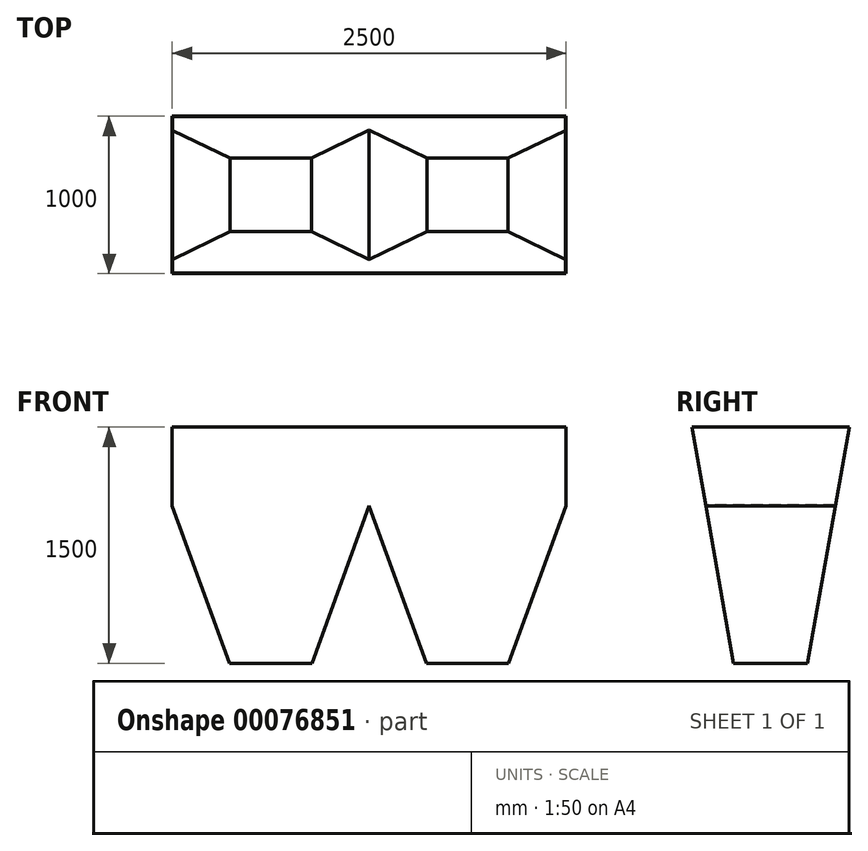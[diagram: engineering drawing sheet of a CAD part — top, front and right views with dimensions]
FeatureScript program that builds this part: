
annotation { "Feature Type Name" : "Feature", "Feature Type Description" : "" }
export const myFeature = defineFeature(function(context is Context, id is Id, definition is map)
    precondition{}
    {
        {
            var Q0;
            Q0=qCreatedBy(makeId("Top.planeOp"),FACE);
            var sketch = newSketch(context, id + "F0", { "sketchPlane" : qUnion([Q0])});
            skLineSegment(sketch, "E0.bottom", {"start": v(-1250, 500) * mm, "end": v(1250, 500) * mm});
            skLineSegment(sketch, "E0.top", {"start": v(-1250, -500) * mm, "end": v(1250, -500) * mm});
            skLineSegment(sketch, "E0.left", {"start": v(-1250, 500) * mm, "end": v(-1250, -500) * mm});
            skLineSegment(sketch, "E0.right", {"start": v(1250, 500) * mm, "end": v(1250, -500) * mm});
            skPoint(sketch, "E0.middle", {"position": v(0, 0) * mm});
            skSolve(sketch);
        }
        {
            var Q0;
            Q0=makeQuery(id+"F0.imprint","IMPRINT",FACE,{"disambiguationData":[TD([[makeQuery(id+"F0.imprint","IMPRINT",EDGE,{"derivedFrom":sQuery(id+"F0.wireOp",EDGE,"E0.bottom")}),-1.0]])]});
            extrude(context, id + "F1", {"entities" : qUnion([Q0]), "depth" : 1500 * mm});
        }
        {
            var Q0;
            Q0=makeQuery(id+"F1.opExtrude","SWEPT_FACE",FACE,{"disambiguationData":[OSD([sQuery(id+"F0.wireOp",EDGE,"E0.top")])]});
            var sketch = newSketch(context, id + "F2", { "sketchPlane" : qUnion([Q0])});
            skLineSegment(sketch, "E1", {"start": v(-1250, 1000) * mm, "end": v(-886.03, 0) * mm});
            skLineSegment(sketch, "E2", {"start": v(-886.03, 0) * mm, "end": v(-1250, 0) * mm});
            skLineSegment(sketch, "E3", {"start": v(-1250, 0) * mm, "end": v(-1250, 1000) * mm});
            skLineSegment(sketch, "E4", {"start": v(-1250, 1000) * mm, "end": v(1250, 1000) * mm, "construction": true});
            skLineSegment(sketch, "E5", {"start": v(1250, 1000) * mm, "end": v(886.03, 0) * mm});
            skLineSegment(sketch, "E6", {"start": v(886.03, 0) * mm, "end": v(1250, 0) * mm});
            skLineSegment(sketch, "E7", {"start": v(1250, 0) * mm, "end": v(1250, 1000) * mm});
            skLineSegment(sketch, "E8", {"start": v(-363.97, 0) * mm, "end": v(0, 1000) * mm});
            skLineSegment(sketch, "E9", {"start": v(0, 1000) * mm, "end": v(363.97, 0) * mm});
            skLineSegment(sketch, "E10", {"start": v(363.97, 0) * mm, "end": v(-363.97, 0) * mm});
            skLineSegment(sketch, "E11", {"start": v(0, 1000) * mm, "end": v(0, 1500) * mm, "construction": true});
            skSolve(sketch);
        }
        {
            var Q0;
            Q0=makeQuery(id+"F2.imprint","IMPRINT",FACE,{"disambiguationData":[TD([[makeQuery(id+"F2.imprint","IMPRINT",EDGE,{"derivedFrom":sQuery(id+"F2.wireOp",EDGE,"E1")}),-1.0]])]});
            var Q1;
            Q1=makeQuery(id+"F2.imprint","IMPRINT",FACE,{"disambiguationData":[TD([[makeQuery(id+"F2.imprint","IMPRINT",EDGE,{"derivedFrom":sQuery(id+"F2.wireOp",EDGE,"E8")}),-1.0]])]});
            var Q2;
            Q2=makeQuery(id+"F2.imprint","IMPRINT",FACE,{"disambiguationData":[TD([[makeQuery(id+"F2.imprint","IMPRINT",EDGE,{"derivedFrom":sQuery(id+"F2.wireOp",EDGE,"E5")}),1.0]])]});
            extrude(context, id + "F3", {"entities" : qUnion([Q0, Q1, Q2]), "operationType" : NewBodyOperationType.REMOVE, "endBound" : BoundingType.THROUGH_ALL, "oppositeDirection" : true, "depth" : 25 * mm});
        }
        {
            var Q0;
            Q0=makeQuery(id+"F1.opExtrude","SWEPT_FACE",FACE,{"disambiguationData":[OSD([sQuery(id+"F0.wireOp",EDGE,"E0.left")])]});
            var sketch = newSketch(context, id + "F4", { "sketchPlane" : qUnion([Q0])});
            skLineSegment(sketch, "E12", {"start": v(-500, 1500) * mm, "end": v(-235.5, 0) * mm});
            skLineSegment(sketch, "E13", {"start": v(-235.5, 0) * mm, "end": v(-500, 0) * mm});
            skLineSegment(sketch, "E14", {"start": v(-500, 0) * mm, "end": v(-500, 1500) * mm});
            skLineSegment(sketch, "E15.MirrorCS", {"start": v(500, 1500) * mm, "end": v(235.5, 0) * mm});
            skLineSegment(sketch, "E16.MirrorCS", {"start": v(235.5, 0) * mm, "end": v(500, 0) * mm});
            skLineSegment(sketch, "E17.MirrorCS", {"start": v(500, 0) * mm, "end": v(500, 1500) * mm});
            skSolve(sketch);
        }
        {
            var Q0;
            {var subQ0=sQuery(id+"F4.wireOp",EDGE,"E13");Q0=makeQuery(id+"F4.imprint","IMPRINT",FACE,{"disambiguationData":[TD([[makeQuery(id+"F4.imprint","IMPRINT",EDGE,{"derivedFrom":subQ0}),-1.0]])]});}
            var Q1;
            {var subQ0=sQuery(id+"F4.wireOp",EDGE,"E14");var subQ1=sQuery(id+"F4.wireOp",EDGE,"E12");var subQ2=sQuery(id+"F0.wireOp",EDGE,"E0.left");var subQ3=makeQuery(id+"F4.imprint","INTERSECT",VERTEX,{"derivedFrom":[makeQuery(id+"F1.opExtrude","CAP_EDGE",EDGE,{"disambiguationData":[OSD([subQ2])],"isStart":false}),subQ1,subQ0]});Q1=makeQuery(id+"F4.imprint","IMPRINT",FACE,{"disambiguationData":[TD([[makeQuery(id+"F4.imprint","IMPRINT",EDGE,{"disambiguationData":[TD([[subQ3,-1.0]])],"derivedFrom":subQ1}),-1.0]])]});}
            var Q2;
            {var subQ0=sQuery(id+"F4.wireOp",EDGE,"E16.MirrorCS");Q2=makeQuery(id+"F4.imprint","IMPRINT",FACE,{"disambiguationData":[TD([[makeQuery(id+"F4.imprint","IMPRINT",EDGE,{"derivedFrom":subQ0}),1.0]])]});}
            var Q3;
            {var subQ0=sQuery(id+"F4.wireOp",EDGE,"E17.MirrorCS");var subQ1=sQuery(id+"F4.wireOp",EDGE,"E15.MirrorCS");var subQ2=sQuery(id+"F0.wireOp",EDGE,"E0.left");var subQ3=makeQuery(id+"F4.imprint","INTERSECT",VERTEX,{"derivedFrom":[makeQuery(id+"F1.opExtrude","CAP_EDGE",EDGE,{"disambiguationData":[OSD([subQ2])],"isStart":false}),subQ1,subQ0]});Q3=makeQuery(id+"F4.imprint","IMPRINT",FACE,{"disambiguationData":[TD([[makeQuery(id+"F4.imprint","IMPRINT",EDGE,{"disambiguationData":[TD([[subQ3,-1.0]])],"derivedFrom":subQ1}),1.0]])]});}
            extrude(context, id + "F5", {"entities" : qUnion([Q0, Q1, Q2, Q3]), "operationType" : NewBodyOperationType.REMOVE, "endBound" : BoundingType.THROUGH_ALL, "oppositeDirection" : true, "depth" : 25 * mm});
        }
        {
            var Q0;
            Q0=makeQuery(id+"F1.opExtrude","CAP_FACE",FACE,{"disambiguationData":[OSD([sQuery(id+"F0.wireOp",EDGE,"E0.bottom"),sQuery(id+"F0.wireOp",EDGE,"E0.top"),sQuery(id+"F0.wireOp",EDGE,"E0.left"),sQuery(id+"F0.wireOp",EDGE,"E0.right")])],"isStart":false});
            var Q1;
            {var subQ0=sQuery(id+"F0.wireOp",EDGE,"E0.bottom");var subQ1=sQuery(id+"F0.wireOp",EDGE,"E0.top");Q1=makeQuery(id+"F3.boolean.opBoolean","SPLIT",FACE,{"disambiguationData":[TD([makeQuery(id+"F3.opExtrude","SWEPT_FACE",FACE,{"disambiguationData":[OSD([sQuery(id+"F2.wireOp",EDGE,"E1")])]})])],"derivedFrom":makeQuery(id+"F1.opExtrude","CAP_FACE",FACE,{"disambiguationData":[OSD([subQ0,subQ1,sQuery(id+"F0.wireOp",EDGE,"E0.left"),sQuery(id+"F0.wireOp",EDGE,"E0.right")])],"isStart":true})});}
            var Q2;
            {var subQ0=sQuery(id+"F0.wireOp",EDGE,"E0.bottom");var subQ1=sQuery(id+"F0.wireOp",EDGE,"E0.top");Q2=makeQuery(id+"F3.boolean.opBoolean","SPLIT",FACE,{"disambiguationData":[TD([makeQuery(id+"F3.opExtrude","SWEPT_FACE",FACE,{"disambiguationData":[OSD([sQuery(id+"F2.wireOp",EDGE,"E5")])]})])],"derivedFrom":makeQuery(id+"F1.opExtrude","CAP_FACE",FACE,{"disambiguationData":[OSD([subQ0,subQ1,sQuery(id+"F0.wireOp",EDGE,"E0.left"),sQuery(id+"F0.wireOp",EDGE,"E0.right")])],"isStart":true})});}
            shell(context, id + "F6", {"entities" : qUnion([Q0, Q1, Q2]), "thickness" : 2.5 * mm});
        }
    });
